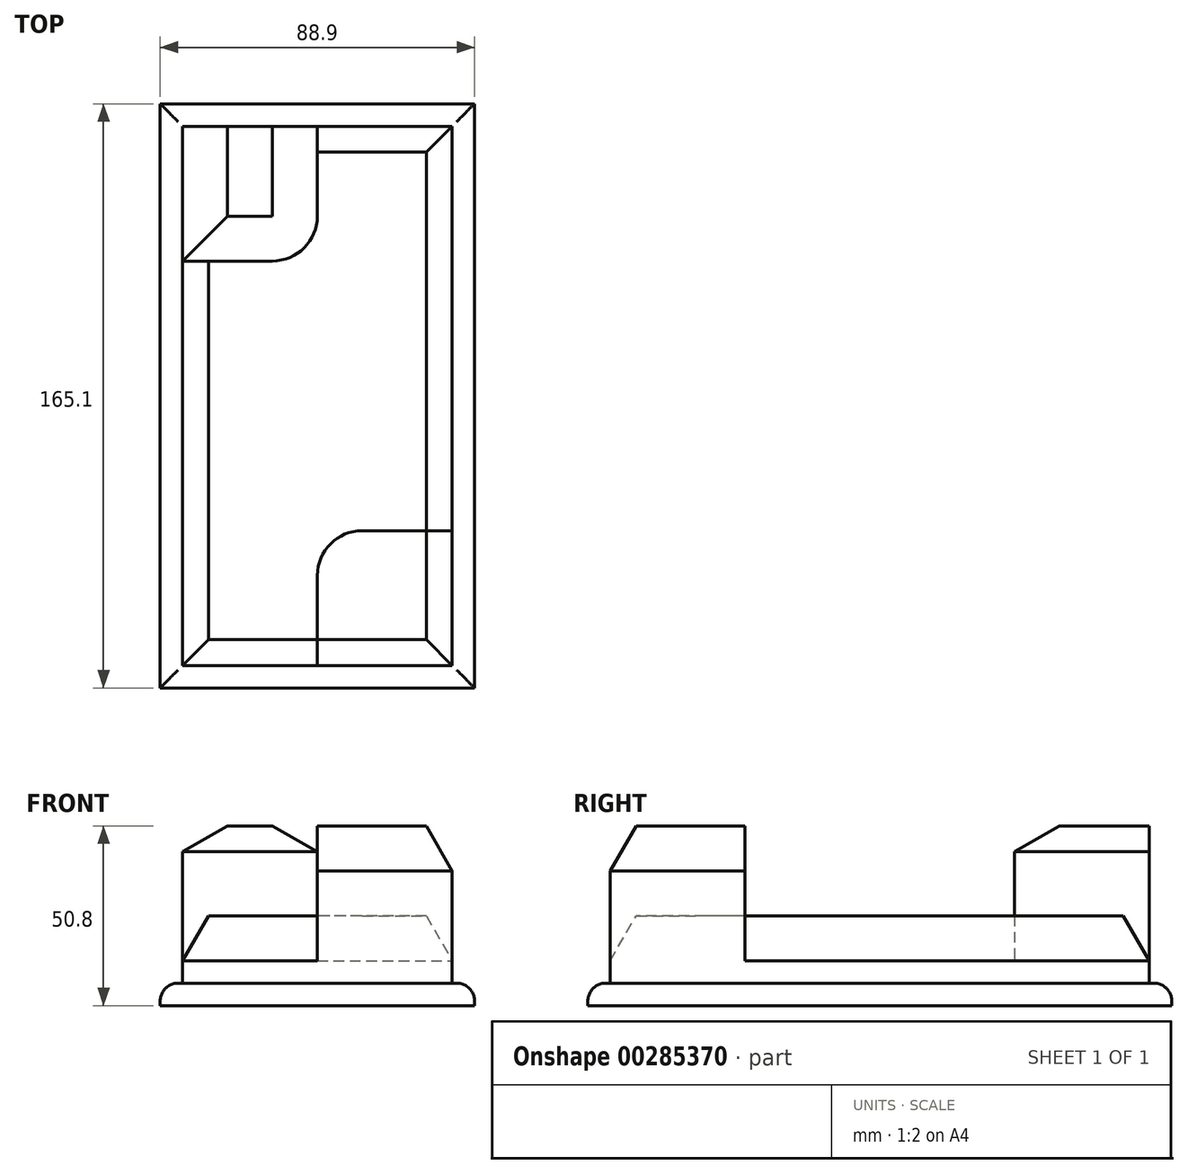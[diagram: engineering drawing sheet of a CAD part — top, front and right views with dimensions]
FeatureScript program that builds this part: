
annotation { "Feature Type Name" : "Feature", "Feature Type Description" : "" }
export const myFeature = defineFeature(function(context is Context, id is Id, definition is map)
    precondition{}
    {
        {
            var Q0;
            Q0=qCreatedBy(makeId("Top.planeOp"),FACE);
            var sketch = newSketch(context, id + "F0", { "sketchPlane" : qUnion([Q0])});
            skLineSegment(sketch, "E0", {"start": v(-53.39, 99.32) * mm, "end": v(22.81, 99.32) * mm});
            skLineSegment(sketch, "E1", {"start": v(22.81, 99.32) * mm, "end": v(22.81, -53.08) * mm});
            skLineSegment(sketch, "E2", {"start": v(22.81, -53.08) * mm, "end": v(-53.39, -53.08) * mm});
            skLineSegment(sketch, "E3", {"start": v(-53.39, -53.08) * mm, "end": v(-53.39, 99.32) * mm});
            skLineSegment(sketch, "E4.0", {"start": v(-59.74, 105.67) * mm, "end": v(29.16, 105.67) * mm});
            skLineSegment(sketch, "E4.1", {"start": v(-59.74, -59.43) * mm, "end": v(-59.74, 105.67) * mm});
            skLineSegment(sketch, "E4.2", {"start": v(29.16, -59.43) * mm, "end": v(-59.74, -59.43) * mm});
            skLineSegment(sketch, "E4.3", {"start": v(29.16, 105.67) * mm, "end": v(29.16, -59.43) * mm});
            skLineSegment(sketch, "E5", {"start": v(-53.39, 61.22) * mm, "end": v(-27.99, 61.22) * mm});
            skLineSegment(sketch, "E6", {"start": v(-15.29, 73.92) * mm, "end": v(-15.29, 99.32) * mm});
            skLineSegment(sketch, "E7", {"start": v(-15.29, -53.08) * mm, "end": v(-15.29, -27.68) * mm});
            skLineSegment(sketch, "E8", {"start": v(-2.59, -14.98) * mm, "end": v(22.81, -14.98) * mm});
            skPoint(sketch, "E9.visualSharp", {"position": v(-15.29, 61.22) * mm});
            skArc(sketch, "E9.filletArc", {"start": v(-27.99, 61.22) * mm, "mid": v(-19, 64.94) * mm, "end": v(-15.29, 73.92) * mm});
            skPoint(sketch, "E10.visualSharp", {"position": v(-15.29, -14.98) * mm});
            skArc(sketch, "E10.filletArc", {"start": v(-2.59, -14.98) * mm, "mid": v(-11.57, -18.7) * mm, "end": v(-15.29, -27.68) * mm});
            skSolve(sketch);
        }
        {
            var Q0;
            Q0=makeQuery(id+"F0.imprint","IMPRINT",FACE,{"disambiguationData":[TD([[makeQuery(id+"F0.imprint","IMPRINT",EDGE,{"derivedFrom":sQuery(id+"F0.wireOp",EDGE,"E4.0")}),-1.0]])]});
            extrude(context, id + "F1", {"entities" : qUnion([Q0]), "depth" : 6.35 * mm});
        }
        {
            var Q0;
            {var subQ9=sQuery(id+"F0.wireOp",EDGE,"E5");Q0=makeQuery(id+"F0.imprint","IMPRINT",FACE,{"disambiguationData":[TD([[makeQuery(id+"F0.imprint","IMPRINT",EDGE,{"derivedFrom":subQ9}),-1.0]])]});}
            extrude(context, id + "F2", {"entities" : qUnion([Q0]), "operationType" : NewBodyOperationType.ADD, "depth" : 25.4 * mm});
        }
        {
            var Q0;
            {var subQ1=sQuery(id+"F0.wireOp",EDGE,"E5");Q0=makeQuery(id+"F0.imprint","IMPRINT",FACE,{"disambiguationData":[TD([[makeQuery(id+"F0.imprint","IMPRINT",EDGE,{"derivedFrom":subQ1}),1.0]])]});}
            var Q1;
            {var subQ4=sQuery(id+"F0.wireOp",EDGE,"E7");Q1=makeQuery(id+"F0.imprint","IMPRINT",FACE,{"disambiguationData":[TD([[makeQuery(id+"F0.imprint","IMPRINT",EDGE,{"derivedFrom":subQ4}),-1.0]])]});}
            extrude(context, id + "F3", {"entities" : qUnion([Q0, Q1]), "operationType" : NewBodyOperationType.ADD, "depth" : 50.8 * mm});
        }
        {
            var Q0;
            Q0=makeQuery(id+"F3.opExtrude","CAP_EDGE",EDGE,{"disambiguationData":[OSD([sQuery(id+"F0.wireOp",EDGE,"E5")])],"isStart":false});
            var Q1;
            Q1=makeQuery(id+"F3.opExtrude","CAP_EDGE",EDGE,{"disambiguationData":[OSD([sQuery(id+"F0.wireOp",EDGE,"E3")])],"isStart":false});
            var Q2;
            Q2=makeQuery(id+"F3.opExtrude","CAP_EDGE",EDGE,{"disambiguationData":[OSD([sQuery(id+"F0.wireOp",EDGE,"E2")])],"isStart":false});
            var Q3;
            Q3=makeQuery(id+"F3.opExtrude","CAP_EDGE",EDGE,{"disambiguationData":[OSD([sQuery(id+"F0.wireOp",EDGE,"E1")])],"isStart":false});
            var Q4;
            Q4=makeQuery(id+"F2.opExtrude","CAP_EDGE",EDGE,{"disambiguationData":[OSD([sQuery(id+"F0.wireOp",EDGE,"E1")])],"isStart":false});
            var Q5;
            Q5=makeQuery(id+"F2.opExtrude","CAP_EDGE",EDGE,{"disambiguationData":[OSD([sQuery(id+"F0.wireOp",EDGE,"E3")])],"isStart":false});
            var Q6;
            Q6=makeQuery(id+"F2.opExtrude","CAP_EDGE",EDGE,{"disambiguationData":[OSD([sQuery(id+"F0.wireOp",EDGE,"E2")])],"isStart":false});
            var Q7;
            Q7=makeQuery(id+"F2.opExtrude","CAP_EDGE",EDGE,{"disambiguationData":[OSD([sQuery(id+"F0.wireOp",EDGE,"E0")])],"isStart":false});
            chamfer(context, id + "F4", {"entities" : qUnion([Q0, Q1, Q2, Q3, Q4, Q5, Q6, Q7]), "chamferType" : ChamferType.OFFSET_ANGLE, "width" : 12.7 * mm, "oppositeDirection" : false, "angle" : 30 * degree, "tangentPropagation" : true});
        }
        {
            var Q0;
            Q0=makeQuery(id+"F1.opExtrude","CAP_EDGE",EDGE,{"disambiguationData":[OSD([sQuery(id+"F0.wireOp",EDGE,"E4.3")])],"isStart":false});
            var Q1;
            Q1=makeQuery(id+"F1.opExtrude","CAP_EDGE",EDGE,{"disambiguationData":[OSD([sQuery(id+"F0.wireOp",EDGE,"E4.2")])],"isStart":false});
            var Q2;
            Q2=makeQuery(id+"F1.opExtrude","CAP_EDGE",EDGE,{"disambiguationData":[OSD([sQuery(id+"F0.wireOp",EDGE,"E4.1")])],"isStart":false});
            var Q3;
            Q3=makeQuery(id+"F1.opExtrude","CAP_EDGE",EDGE,{"disambiguationData":[OSD([sQuery(id+"F0.wireOp",EDGE,"E4.0")])],"isStart":false});
            fillet(context, id + "F5", {"entities" : qUnion([Q0, Q1, Q2, Q3]), "radius" : 5.08 * mm, "tangentPropagation" : true, "allowEdgeOverflow" : false});
        }
    });
